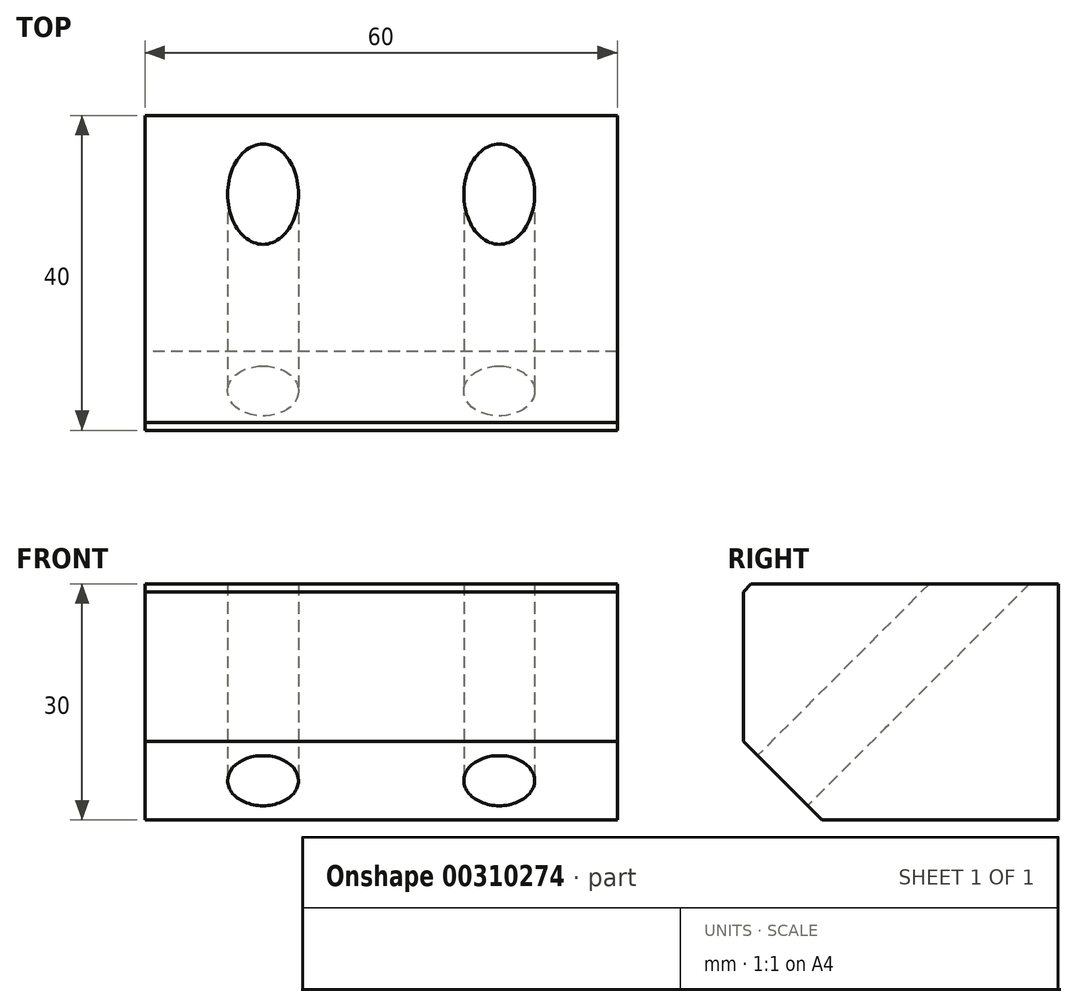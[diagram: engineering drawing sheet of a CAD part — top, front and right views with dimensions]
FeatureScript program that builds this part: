
annotation { "Feature Type Name" : "Feature", "Feature Type Description" : "" }
export const myFeature = defineFeature(function(context is Context, id is Id, definition is map)
    precondition{}
    {
        {
            var Q0;
            Q0=qCreatedBy(makeId("Top.planeOp"),FACE);
            var sketch = newSketch(context, id + "F0", { "sketchPlane" : qUnion([Q0])});
            skLineSegment(sketch, "E0.bottom", {"start": v(0, 0) * mm, "end": v(60, 0) * mm});
            skLineSegment(sketch, "E0.top", {"start": v(0, 40) * mm, "end": v(60, 40) * mm});
            skLineSegment(sketch, "E0.left", {"start": v(0, 0) * mm, "end": v(0, 40) * mm});
            skLineSegment(sketch, "E0.right", {"start": v(60, 0) * mm, "end": v(60, 40) * mm});
            skSolve(sketch);
        }
        {
            var Q0;
            Q0=makeQuery(id+"F0.imprint","IMPRINT",FACE,{"disambiguationData":[TD([[makeQuery(id+"F0.imprint","IMPRINT",EDGE,{"derivedFrom":sQuery(id+"F0.wireOp",EDGE,"E0.bottom")}),1.0]])]});
            extrude(context, id + "F1", {"entities" : qUnion([Q0]), "oppositeDirection" : true, "depth" : 30 * mm});
        }
        {
            var Q0;
            Q0=makeQuery(id+"F1.opExtrude","CAP_EDGE",EDGE,{"disambiguationData":[OSD([sQuery(id+"F0.wireOp",EDGE,"E0.bottom")])],"isStart":false});
            chamfer(context, id + "F2", {"entities" : qUnion([Q0]), "width" : 10 * mm, "tangentPropagation" : true});
        }
        {
            var Q0;
            Q0=makeQuery(id+"F2.opChamfer","BLEND_FACE",FACE,{"disambiguationData":[OSD([sQuery(id+"F0.wireOp",EDGE,"E0.bottom")])]});
            var sketch = newSketch(context, id + "F3", { "sketchPlane" : qUnion([Q0])});
            skPoint(sketch, "E1", {"position": v(0, -21.21) * mm});
            skPoint(sketch, "E2", {"position": v(15, -21.21) * mm});
            skPoint(sketch, "E3", {"position": v(45, -21.21) * mm});
            skPoint(sketch, "E4", {"position": v(60, -21.21) * mm});
            skSolve(sketch);
        }
        {
            var Q0;
            Q0=sQuery(id+"F3.wireOp",VERTEX,"E2");
            var Q1;
            Q1=sQuery(id+"F3.wireOp",VERTEX,"E3");
            var Q2;
            Q2=makeQuery(id+"F1.opExtrude","SWEPT_BODY",BODY,{"disambiguationData":[OSD([sQuery(id+"F0.wireOp",EDGE,"E0.bottom"),sQuery(id+"F0.wireOp",EDGE,"E0.top"),sQuery(id+"F0.wireOp",EDGE,"E0.left"),sQuery(id+"F0.wireOp",EDGE,"E0.right")])]});
            hole(context, id + "F4", {"style" : HoleStyle.SIMPLE, "endStyle" : HoleEndStyle.THROUGH, "standardTappedOrClearance" : lookupTablePath({ "standard" : "ISO", "engagement" : "75%", "pitch" : "1 mm", "size" : "M10", "type" : "Tapped" }), "standardBlindInLast" : lookupTablePath({ "standard" : "ISO", "engagement" : "75%", "pitch" : "1 mm", "size" : "M10", "type" : "Tapped" }), "holeDiameter" : 9 * mm, "showTappedDepth" : true, "tappedDepth" : 12 * mm, "tapClearance" : 3, "locations" : qUnion([Q0, Q1]), "scope" : qUnion([Q2]), "majorDiameter" : 10 * mm});
        }
        {
            var Q0;
            Q0=makeQuery(id+"F1.opExtrude","CAP_EDGE",EDGE,{"disambiguationData":[OSD([sQuery(id+"F0.wireOp",EDGE,"E0.bottom")])],"isStart":true});
            chamfer(context, id + "F5", {"entities" : qUnion([Q0]), "width" : 1 * mm, "tangentPropagation" : true});
        }
    });
